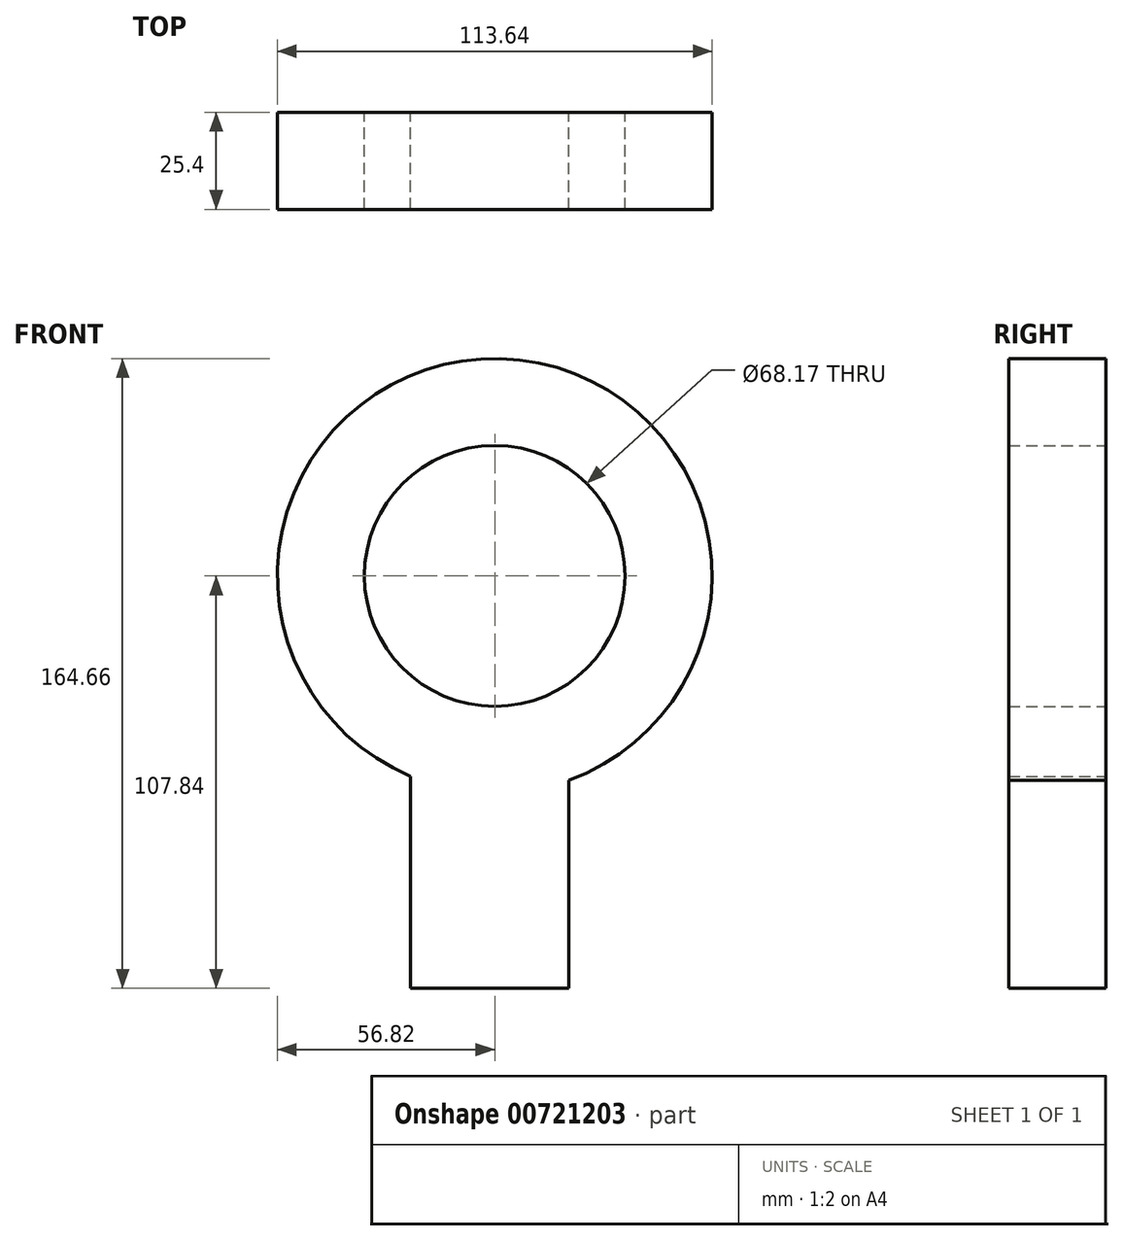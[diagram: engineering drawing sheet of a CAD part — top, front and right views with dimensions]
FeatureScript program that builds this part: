
annotation { "Feature Type Name" : "Feature", "Feature Type Description" : "" }
export const myFeature = defineFeature(function(context is Context, id is Id, definition is map)
    precondition{}
    {
        {
            var Q0;
            Q0=qCreatedBy(makeId("Front.planeOp"),FACE);
            var sketch = newSketch(context, id + "F0", { "sketchPlane" : qUnion([Q0])});
            skCircle(sketch, "E0", {"center": v(0, 0) * mm, "radius": 34.08 * mm});
            skCircle(sketch, "E1", {"center": v(0, 0) * mm, "radius": 56.82 * mm});
            skLineSegment(sketch, "E2.bottom", {"start": v(-22.07, -44.11) * mm, "end": v(19.34, -44.11) * mm});
            skLineSegment(sketch, "E2.top", {"start": v(-22.07, -107.84) * mm, "end": v(19.34, -107.84) * mm});
            skLineSegment(sketch, "E2.left", {"start": v(-22.07, -44.11) * mm, "end": v(-22.07, -107.84) * mm});
            skLineSegment(sketch, "E2.right", {"start": v(19.34, -44.11) * mm, "end": v(19.34, -107.84) * mm});
            skSolve(sketch);
        }
        {
            var Q0;
            Q0 = qSketchRegion(id + "F0", true);
            extrude(context, id + "F1", {"entities" : qUnion([Q0]), "depth" : 25.4 * mm, "offsetDistance" : 25.4 * mm});
        }
    });
